FREECAD ASSEMBLY — COMPONENT RECIPES ("Assembly")

This assembly document has 52 components, labeled P0..P51 below (a component is one placed body or linked part). 0 of them carry a construction recipe — the FreeCAD feature program that regenerates the part from scratch, quoted from this document or its linked companion documents; the rest are supplied as boundary geometry only. No exploded tour is included for this assembly.
COMPONENT P0 — geometry summary ("Collar002"; no construction recipe available for this part):
  bounding box: 45.3 x 45.3 x 5.0 mm
  tessellated surface: 1,776 triangles
  volume: 1072 mm^3 (10% of its bounding box)
  symmetry: 6-fold rotationally symmetric about the z axis; mirror-symmetric across its x mid-plane
COMPONENT P1 — geometry summary ("Collar003"; no construction recipe available for this part):
  bounding box: 45.3 x 45.3 x 5.0 mm
  tessellated surface: 1,776 triangles
  volume: 1072 mm^3 (10% of its bounding box)
  symmetry: 6-fold rotationally symmetric about the z axis; mirror-symmetric across its x mid-plane
COMPONENT P2 — geometry summary ("Pillar025"; no construction recipe available for this part):
  bounding box: 158.4 x 4.5 x 2.0 mm
  tessellated surface: 180 triangles
  volume: 874 mm^3 (59% of its bounding box)
  symmetry: mirror-symmetric across its x mid-plane
COMPONENT P3 — geometry summary ("Pillar026"; no construction recipe available for this part):
  bounding box: 158.4 x 4.6 x 2.9 mm
  tessellated surface: 180 triangles
  volume: 874 mm^3 (41% of its bounding box)
  symmetry: mirror-symmetric across its x mid-plane
COMPONENT P4 — geometry summary ("Pillar027"; no construction recipe available for this part):
  bounding box: 158.4 x 4.4 x 3.6 mm
  tessellated surface: 180 triangles
  volume: 874 mm^3 (34% of its bounding box)
  symmetry: 2-fold rotationally symmetric about the z axis
COMPONENT P5 — geometry summary ("Pillar028"; no construction recipe available for this part):
  bounding box: 158.4 x 4.1 x 4.1 mm
  tessellated surface: 180 triangles
  volume: 874 mm^3 (33% of its bounding box)
COMPONENT P6 — geometry summary ("Pillar029"; no construction recipe available for this part):
  bounding box: 158.4 x 4.4 x 3.6 mm
  tessellated surface: 180 triangles
  volume: 874 mm^3 (34% of its bounding box)
  symmetry: 2-fold rotationally symmetric about the z axis
COMPONENT P7 — geometry summary ("Pillar030"; no construction recipe available for this part):
  bounding box: 158.4 x 4.6 x 2.9 mm
  tessellated surface: 180 triangles
  volume: 874 mm^3 (41% of its bounding box)
COMPONENT P8 — geometry summary ("Pillar031"; no construction recipe available for this part):
  bounding box: 158.4 x 4.5 x 2.0 mm
  tessellated surface: 180 triangles
  volume: 874 mm^3 (59% of its bounding box)
  symmetry: mirror-symmetric across its y mid-plane
COMPONENT P9 — geometry summary ("Pillar032"; no construction recipe available for this part):
  bounding box: 158.4 x 4.6 x 2.9 mm
  tessellated surface: 180 triangles
  volume: 874 mm^3 (41% of its bounding box)
  symmetry: mirror-symmetric across its y mid-plane
COMPONENT P10 — geometry summary ("Pillar033"; no construction recipe available for this part):
  bounding box: 158.4 x 4.4 x 3.6 mm
  tessellated surface: 180 triangles
  volume: 874 mm^3 (34% of its bounding box)
  symmetry: 2-fold rotationally symmetric about the z axis
COMPONENT P11 — geometry summary ("Pillar034"; no construction recipe available for this part):
  bounding box: 158.4 x 4.1 x 4.1 mm
  tessellated surface: 180 triangles
  volume: 874 mm^3 (33% of its bounding box)
COMPONENT P12 — geometry summary ("Pillar035"; no construction recipe available for this part):
  bounding box: 158.4 x 4.4 x 3.6 mm
  tessellated surface: 180 triangles
  volume: 874 mm^3 (34% of its bounding box)
  symmetry: 2-fold rotationally symmetric about the z axis
COMPONENT P13 — geometry summary ("Pillar036"; no construction recipe available for this part):
  bounding box: 158.4 x 4.6 x 2.9 mm
  tessellated surface: 180 triangles
  volume: 874 mm^3 (41% of its bounding box)
COMPONENT P14 — geometry summary ("Pillar037"; no construction recipe available for this part):
  bounding box: 158.4 x 4.5 x 2.0 mm
  tessellated surface: 180 triangles
  volume: 874 mm^3 (59% of its bounding box)
  symmetry: mirror-symmetric across its x mid-plane
COMPONENT P15 — geometry summary ("Pillar038"; no construction recipe available for this part):
  bounding box: 158.4 x 4.6 x 2.9 mm
  tessellated surface: 180 triangles
  volume: 874 mm^3 (41% of its bounding box)
  symmetry: mirror-symmetric across its x mid-plane
COMPONENT P16 — geometry summary ("Pillar039"; no construction recipe available for this part):
  bounding box: 158.4 x 4.4 x 3.6 mm
  tessellated surface: 180 triangles
  volume: 874 mm^3 (34% of its bounding box)
  symmetry: 2-fold rotationally symmetric about the z axis
COMPONENT P17 — geometry summary ("Pillar040"; no construction recipe available for this part):
  bounding box: 158.4 x 4.1 x 4.1 mm
  tessellated surface: 180 triangles
  volume: 874 mm^3 (33% of its bounding box)
COMPONENT P18 — geometry summary ("Pillar041"; no construction recipe available for this part):
  bounding box: 158.4 x 4.4 x 3.6 mm
  tessellated surface: 180 triangles
  volume: 874 mm^3 (34% of its bounding box)
  symmetry: 2-fold rotationally symmetric about the z axis
COMPONENT P19 — geometry summary ("Pillar042"; no construction recipe available for this part):
  bounding box: 158.4 x 4.6 x 2.9 mm
  tessellated surface: 180 triangles
  volume: 874 mm^3 (41% of its bounding box)
COMPONENT P20 — geometry summary ("Pillar043"; no construction recipe available for this part):
  bounding box: 158.4 x 4.5 x 2.0 mm
  tessellated surface: 180 triangles
  volume: 874 mm^3 (59% of its bounding box)
  symmetry: mirror-symmetric across its y mid-plane
COMPONENT P21 — geometry summary ("Pillar044"; no construction recipe available for this part):
  bounding box: 158.4 x 4.6 x 2.9 mm
  tessellated surface: 180 triangles
  volume: 874 mm^3 (41% of its bounding box)
  symmetry: mirror-symmetric across its y mid-plane
COMPONENT P22 — geometry summary ("Pillar045"; no construction recipe available for this part):
  bounding box: 158.4 x 4.4 x 3.6 mm
  tessellated surface: 180 triangles
  volume: 874 mm^3 (34% of its bounding box)
  symmetry: 2-fold rotationally symmetric about the z axis
COMPONENT P23 — geometry summary ("Pillar046"; no construction recipe available for this part):
  bounding box: 158.4 x 4.1 x 4.1 mm
  tessellated surface: 180 triangles
  volume: 874 mm^3 (33% of its bounding box)
COMPONENT P24 — geometry summary ("Pillar047"; no construction recipe available for this part):
  bounding box: 158.4 x 4.4 x 3.6 mm
  tessellated surface: 180 triangles
  volume: 874 mm^3 (34% of its bounding box)
  symmetry: 2-fold rotationally symmetric about the z axis
COMPONENT P25 — geometry summary ("Pillar048"; no construction recipe available for this part):
  bounding box: 158.4 x 4.6 x 2.9 mm
  tessellated surface: 180 triangles
  volume: 874 mm^3 (41% of its bounding box)
COMPONENT P26 — geometry summary ("Pillar049"; no construction recipe available for this part):
  bounding box: 158.4 x 4.5 x 2.0 mm
  tessellated surface: 180 triangles
  volume: 874 mm^3 (59% of its bounding box)
  symmetry: mirror-symmetric across its x mid-plane
COMPONENT P27 — geometry summary ("Pillar050"; no construction recipe available for this part):
  bounding box: 158.4 x 4.6 x 2.9 mm
  tessellated surface: 180 triangles
  volume: 874 mm^3 (41% of its bounding box)
  symmetry: mirror-symmetric across its x mid-plane
COMPONENT P28 — geometry summary ("Pillar051"; no construction recipe available for this part):
  bounding box: 158.4 x 4.4 x 3.6 mm
  tessellated surface: 180 triangles
  volume: 874 mm^3 (34% of its bounding box)
  symmetry: 2-fold rotationally symmetric about the z axis
COMPONENT P29 — geometry summary ("Pillar052"; no construction recipe available for this part):
  bounding box: 158.4 x 4.1 x 4.1 mm
  tessellated surface: 180 triangles
  volume: 874 mm^3 (33% of its bounding box)
COMPONENT P30 — geometry summary ("Pillar053"; no construction recipe available for this part):
  bounding box: 158.4 x 4.4 x 3.6 mm
  tessellated surface: 180 triangles
  volume: 874 mm^3 (34% of its bounding box)
  symmetry: 2-fold rotationally symmetric about the z axis
COMPONENT P31 — geometry summary ("Pillar054"; no construction recipe available for this part):
  bounding box: 158.4 x 4.6 x 2.9 mm
  tessellated surface: 180 triangles
  volume: 874 mm^3 (41% of its bounding box)
COMPONENT P32 — geometry summary ("Pillar055"; no construction recipe available for this part):
  bounding box: 158.4 x 4.5 x 2.0 mm
  tessellated surface: 180 triangles
  volume: 874 mm^3 (59% of its bounding box)
  symmetry: mirror-symmetric across its y mid-plane
COMPONENT P33 — geometry summary ("Pillar056"; no construction recipe available for this part):
  bounding box: 158.4 x 4.6 x 2.9 mm
  tessellated surface: 180 triangles
  volume: 874 mm^3 (41% of its bounding box)
  symmetry: mirror-symmetric across its y mid-plane
COMPONENT P34 — geometry summary ("Pillar057"; no construction recipe available for this part):
  bounding box: 158.4 x 4.4 x 3.6 mm
  tessellated surface: 180 triangles
  volume: 874 mm^3 (34% of its bounding box)
  symmetry: 2-fold rotationally symmetric about the z axis
COMPONENT P35 — geometry summary ("Pillar058"; no construction recipe available for this part):
  bounding box: 158.4 x 4.1 x 4.1 mm
  tessellated surface: 180 triangles
  volume: 874 mm^3 (33% of its bounding box)
COMPONENT P36 — geometry summary ("Pillar059"; no construction recipe available for this part):
  bounding box: 158.4 x 4.4 x 3.6 mm
  tessellated surface: 180 triangles
  volume: 874 mm^3 (34% of its bounding box)
  symmetry: 2-fold rotationally symmetric about the z axis
COMPONENT P37 — geometry summary ("Pillar060"; no construction recipe available for this part):
  bounding box: 158.4 x 4.6 x 2.9 mm
  tessellated surface: 180 triangles
  volume: 874 mm^3 (41% of its bounding box)
COMPONENT P38 — geometry summary ("Pillar061"; no construction recipe available for this part):
  bounding box: 158.4 x 4.5 x 2.0 mm
  tessellated surface: 180 triangles
  volume: 874 mm^3 (59% of its bounding box)
  symmetry: mirror-symmetric across its x mid-plane
COMPONENT P39 — geometry summary ("Pillar062"; no construction recipe available for this part):
  bounding box: 158.4 x 4.6 x 2.9 mm
  tessellated surface: 180 triangles
  volume: 874 mm^3 (41% of its bounding box)
  symmetry: mirror-symmetric across its x mid-plane
COMPONENT P40 — geometry summary ("Pillar063"; no construction recipe available for this part):
  bounding box: 158.4 x 4.4 x 3.6 mm
  tessellated surface: 180 triangles
  volume: 874 mm^3 (34% of its bounding box)
  symmetry: 2-fold rotationally symmetric about the z axis
COMPONENT P41 — geometry summary ("Pillar064"; no construction recipe available for this part):
  bounding box: 158.4 x 4.1 x 4.1 mm
  tessellated surface: 180 triangles
  volume: 874 mm^3 (33% of its bounding box)
COMPONENT P42 — geometry summary ("Pillar065"; no construction recipe available for this part):
  bounding box: 158.4 x 4.4 x 3.6 mm
  tessellated surface: 180 triangles
  volume: 874 mm^3 (34% of its bounding box)
  symmetry: 2-fold rotationally symmetric about the z axis
COMPONENT P43 — geometry summary ("Pillar066"; no construction recipe available for this part):
  bounding box: 158.4 x 4.6 x 2.9 mm
  tessellated surface: 180 triangles
  volume: 874 mm^3 (41% of its bounding box)
COMPONENT P44 — geometry summary ("Pillar067"; no construction recipe available for this part):
  bounding box: 158.4 x 4.5 x 2.0 mm
  tessellated surface: 180 triangles
  volume: 874 mm^3 (59% of its bounding box)
  symmetry: mirror-symmetric across its y mid-plane
COMPONENT P45 — geometry summary ("Pillar068"; no construction recipe available for this part):
  bounding box: 158.4 x 4.6 x 2.9 mm
  tessellated surface: 180 triangles
  volume: 874 mm^3 (41% of its bounding box)
  symmetry: mirror-symmetric across its y mid-plane
COMPONENT P46 — geometry summary ("Pillar069"; no construction recipe available for this part):
  bounding box: 158.4 x 4.4 x 3.6 mm
  tessellated surface: 180 triangles
  volume: 874 mm^3 (34% of its bounding box)
  symmetry: 2-fold rotationally symmetric about the z axis
COMPONENT P47 — geometry summary ("Pillar070"; no construction recipe available for this part):
  bounding box: 158.4 x 4.1 x 4.1 mm
  tessellated surface: 180 triangles
  volume: 874 mm^3 (33% of its bounding box)
COMPONENT P48 — geometry summary ("Pillar071"; no construction recipe available for this part):
  bounding box: 158.4 x 4.4 x 3.6 mm
  tessellated surface: 180 triangles
  volume: 874 mm^3 (34% of its bounding box)
  symmetry: 2-fold rotationally symmetric about the z axis
COMPONENT P49 — geometry summary ("Pillar072"; no construction recipe available for this part):
  bounding box: 158.4 x 4.6 x 2.9 mm
  tessellated surface: 180 triangles
  volume: 874 mm^3 (41% of its bounding box)
COMPONENT P50 — geometry summary ("Top002"; no construction recipe available for this part):
  bounding box: 78.0 x 45.3 x 45.3 mm
  tessellated surface: 2,280 triangles
  volume: 27171 mm^3 (17% of its bounding box)
  symmetry: revolution-symmetric about the z axis through its bounding-box center; mirror-symmetric across its x mid-plane
COMPONENT P51 — geometry summary ("Top003"; no construction recipe available for this part):
  bounding box: 78.0 x 45.3 x 45.3 mm
  tessellated surface: 2,280 triangles
  volume: 27171 mm^3 (17% of its bounding box)
  symmetry: revolution-symmetric about the z axis through its bounding-box center; mirror-symmetric across its x mid-plane
PROVENANCE & LICENSES
A FreeCAD (.FCStd) document from a public repository crawl; recipes are the document's own serialized feature recipes (and, for linked parts, companion documents' recipes).
License: as declared in the source repository (recorded in the dataset sidecar).
